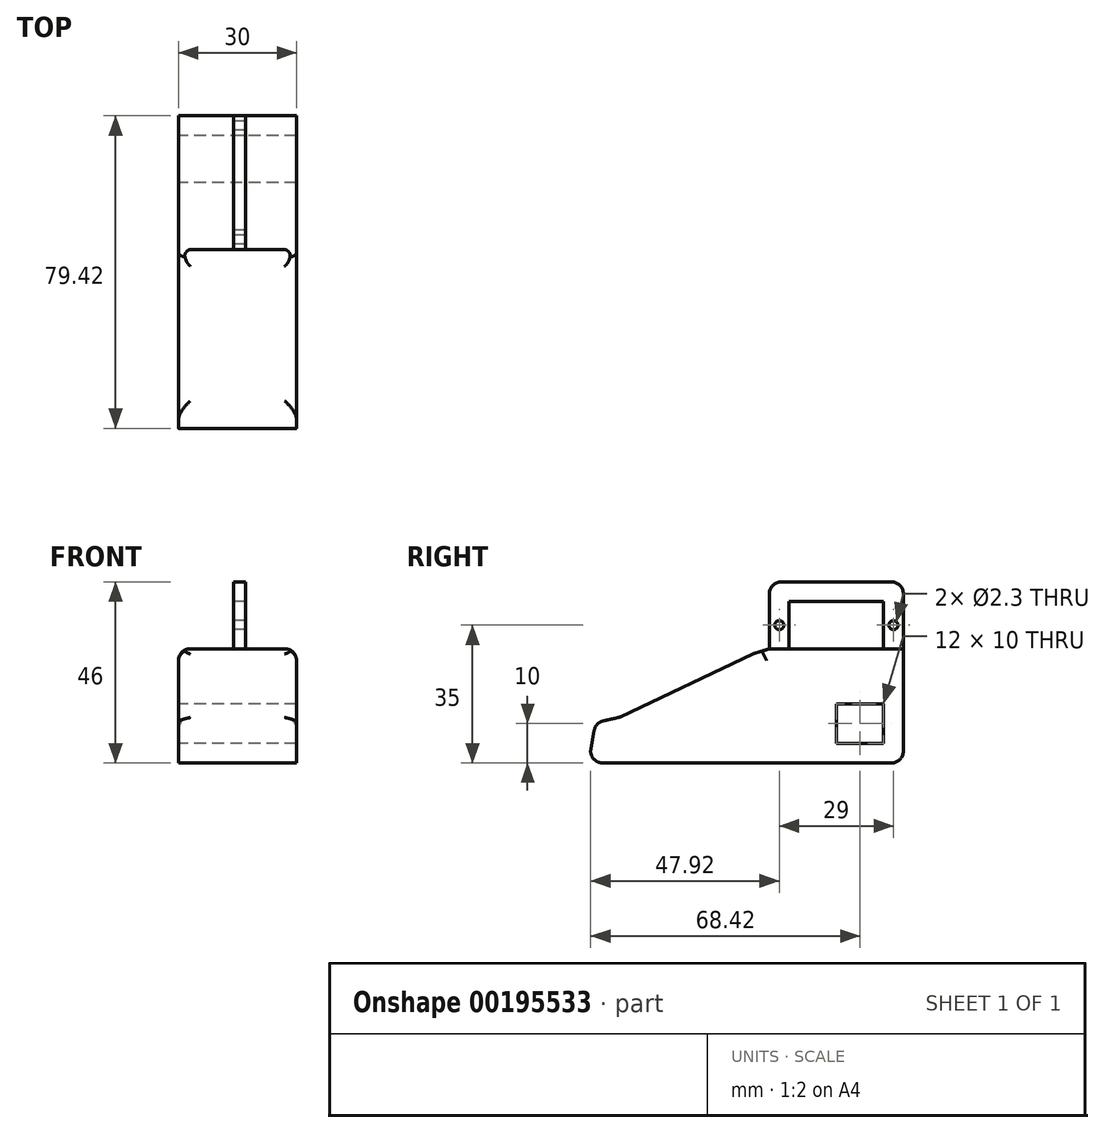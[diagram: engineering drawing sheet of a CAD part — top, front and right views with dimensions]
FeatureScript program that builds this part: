
annotation { "Feature Type Name" : "Feature", "Feature Type Description" : "" }
export const myFeature = defineFeature(function(context is Context, id is Id, definition is map)
    precondition{}
    {
        {
            var Q0;
            Q0=qCreatedBy(makeId("Right.planeOp"),FACE);
            var sketch = newSketch(context, id + "F0", { "sketchPlane" : qUnion([Q0])});
            skLineSegment(sketch, "E0.bottom", {"start": v(-12, 6) * mm, "end": v(12, 6) * mm});
            skLineSegment(sketch, "E0.top", {"start": v(-12, -6) * mm, "end": v(12, -6) * mm});
            skLineSegment(sketch, "E0.left", {"start": v(-12, 6) * mm, "end": v(-12, -6) * mm});
            skLineSegment(sketch, "E0.right", {"start": v(12, 6) * mm, "end": v(12, -6) * mm});
            skPoint(sketch, "E0.middle", {"position": v(0, 0) * mm});
            skLineSegment(sketch, "E1", {"start": v(-17, -6) * mm, "end": v(-17, 8) * mm});
            skLineSegment(sketch, "E2", {"start": v(-14, 11) * mm, "end": v(0, 11) * mm});
            skLineSegment(sketch, "E3", {"start": v(17, -32) * mm, "end": v(17, 8) * mm});
            skLineSegment(sketch, "E4", {"start": v(14, 11) * mm, "end": v(0, 11) * mm});
            skLineSegment(sketch, "E5", {"start": v(0, 6) * mm, "end": v(0, 11) * mm, "construction": true});
            skLineSegment(sketch, "E6", {"start": v(-17, 2.5) * mm, "end": v(-12, 2.5) * mm, "construction": true});
            skLineSegment(sketch, "E7", {"start": v(-17, 0) * mm, "end": v(-12, 0) * mm, "construction": true});
            skLineSegment(sketch, "E8", {"start": v(12, 0) * mm, "end": v(17, 0) * mm, "construction": true});
            skCircle(sketch, "E9", {"center": v(-14.5, 0) * mm, "radius": 1.15 * mm});
            skCircle(sketch, "E10", {"center": v(14.5, 0) * mm, "radius": 1.15 * mm});
            skLineSegment(sketch, "E11", {"start": v(-59.42, -35) * mm, "end": v(14, -35) * mm});
            skLineSegment(sketch, "E12", {"start": v(0, -6) * mm, "end": v(12, -6) * mm, "construction": true});
            skLineSegment(sketch, "E13.bottom", {"start": v(12, -20) * mm, "end": v(0, -20) * mm});
            skLineSegment(sketch, "E13.top", {"start": v(12, -30) * mm, "end": v(0, -30) * mm});
            skLineSegment(sketch, "E13.left", {"start": v(12, -20) * mm, "end": v(12, -30) * mm});
            skLineSegment(sketch, "E13.right", {"start": v(0, -20) * mm, "end": v(0, -30) * mm});
            skLineSegment(sketch, "E14", {"start": v(0, -20) * mm, "end": v(12, -30) * mm, "construction": true});
            skLineSegment(sketch, "E15", {"start": v(6, -25) * mm, "end": v(6, -6) * mm, "construction": true});
            skLineSegment(sketch, "E16", {"start": v(6, -30) * mm, "end": v(6, -35) * mm, "construction": true});
            skLineSegment(sketch, "E17", {"start": v(-17, -6) * mm, "end": v(-12, -6) * mm});
            skLineSegment(sketch, "E18", {"start": v(17, -6) * mm, "end": v(12, -6) * mm});
            skLineSegment(sketch, "E19", {"start": v(0, 0) * mm, "end": v(12, 0) * mm, "construction": true});
            skLineSegment(sketch, "E20", {"start": v(6, 0) * mm, "end": v(6, -20) * mm, "construction": true});
            skLineSegment(sketch, "E21", {"start": v(-62.38, -31.48) * mm, "end": v(-61.54, -26.74) * mm});
            skPoint(sketch, "E22.endSnap0", {"position": v(6, -32.5) * mm});
            skLineSegment(sketch, "E23", {"start": v(-63, -35) * mm, "end": v(6, -46.81) * mm, "construction": true});
            skCircle(sketch, "E24", {"center": v(6, -25) * mm, "radius": 21.5 * mm, "construction": true});
            skPoint(sketch, "E25.visualSharp", {"position": v(-63, -35) * mm});
            skArc(sketch, "E25.filletArc", {"start": v(-62.38, -31.48) * mm, "mid": v(-61.72, -33.93) * mm, "end": v(-59.42, -35) * mm});
            skPoint(sketch, "E26.visualSharp", {"position": v(-61.26, -25.15) * mm});
            skArc(sketch, "E26.filletArc", {"start": v(-59.26, -24.34) * mm, "mid": v(-60.76, -25.2) * mm, "end": v(-61.54, -26.74) * mm});
            skPoint(sketch, "E27.visualSharp", {"position": v(17, -35) * mm});
            skArc(sketch, "E27.filletArc", {"start": v(14, -35) * mm, "mid": v(16.12, -34.12) * mm, "end": v(17, -32) * mm});
            skPoint(sketch, "E28.visualSharp", {"position": v(-17, 11) * mm});
            skArc(sketch, "E28.filletArc", {"start": v(-14, 11) * mm, "mid": v(-16.12, 10.12) * mm, "end": v(-17, 8) * mm});
            skPoint(sketch, "E29.visualSharp", {"position": v(17, 11) * mm});
            skArc(sketch, "E29.filletArc", {"start": v(17, 8) * mm, "mid": v(16.12, 10.12) * mm, "end": v(14, 11) * mm});
            skLineSegment(sketch, "E30", {"start": v(-59.26, -24.34) * mm, "end": v(-55.12, -23.4) * mm});
            skLineSegment(sketch, "E31", {"start": v(-55.12, -23.4) * mm, "end": v(-21, -7.22) * mm});
            skLineSegment(sketch, "E32", {"start": v(-21, -7.22) * mm, "end": v(-17, -6) * mm});
            skSolve(sketch);
        }
        {
            var Q0;
            Q0=makeQuery(id+"F0.imprint","IMPRINT",FACE,{"disambiguationData":[TD([[makeQuery(id+"F0.imprint","IMPRINT",EDGE,{"derivedFrom":sQuery(id+"F0.wireOp",EDGE,"E0.top")}),-1.0]])]});
            extrude(context, id + "F1", {"entities" : qUnion([Q0]), "depth" : 16 * mm});
        }
        {
            var Q0;
            Q0=makeQuery(id+"F0.imprint","IMPRINT",FACE,{"disambiguationData":[TD([[makeQuery(id+"F0.imprint","IMPRINT",EDGE,{"derivedFrom":sQuery(id+"F0.wireOp",EDGE,"E0.bottom")}),1.0]])]});
            extrude(context, id + "F2", {"entities" : qUnion([Q0]), "operationType" : NewBodyOperationType.ADD, "depth" : 3 * mm});
        }
        {
            var Q0;
            Q0=makeQuery(id+"F0.imprint","IMPRINT",FACE,{"disambiguationData":[TD([[makeQuery(id+"F0.imprint","IMPRINT",EDGE,{"derivedFrom":sQuery(id+"F0.wireOp",EDGE,"E0.top")}),-1.0]])]});
            extrude(context, id + "F3", {"entities" : qUnion([Q0]), "operationType" : NewBodyOperationType.ADD, "oppositeDirection" : true, "depth" : 14 * mm});
        }
        {
            var Q0;
            {var subQ0=sQuery(id+"F0.wireOp",EDGE,"E31");Q0=makeQuery(id+"F3.boolean.opBoolean","MERGE",FACE,{"derivedFrom":[makeQuery(id+"F1.opExtrude","SWEPT_FACE",FACE,{"disambiguationData":[OSD([subQ0])]}),makeQuery(id+"F3.opExtrude","SWEPT_FACE",FACE,{"disambiguationData":[OSD([subQ0])]})]});}
            fillet(context, id + "F4", {"entities" : qUnion([Q0]), "radius" : 3 * mm, "tangentPropagation" : true, "allowEdgeOverflow" : false});
        }
        {
            var Q0;
            Q0=makeQuery(id+"F3.opExtrude","CAP_EDGE",EDGE,{"disambiguationData":[OSD([sQuery(id+"F0.wireOp",EDGE,"E0.top"),sQuery(id+"F0.wireOp",EDGE,"E17"),sQuery(id+"F0.wireOp",EDGE,"E18")])],"isStart":false});
            var Q1;
            Q1=makeQuery(id+"F1.opExtrude","CAP_EDGE",EDGE,{"disambiguationData":[OSD([sQuery(id+"F0.wireOp",EDGE,"E0.top"),sQuery(id+"F0.wireOp",EDGE,"E17"),sQuery(id+"F0.wireOp",EDGE,"E18")])],"isStart":false});
            fillet(context, id + "F5", {"entities" : qUnion([Q0, Q1]), "radius" : 3 * mm, "tangentPropagation" : true, "allowEdgeOverflow" : false});
        }
    });
